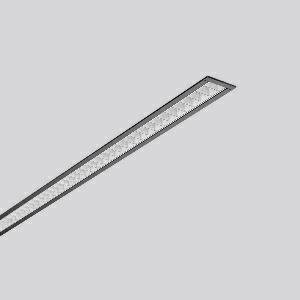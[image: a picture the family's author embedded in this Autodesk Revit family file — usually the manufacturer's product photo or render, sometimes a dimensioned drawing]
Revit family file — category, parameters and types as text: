
# Revit family: less_is_more_27_312177_003_1_6459
name_source: partatom
category: Lighting Fixtures
units: mm (PartAtom-declared; Revit-internal decimal feet)

## family parameters
Cut with Voids When Loaded = No
Host = Face
Light Source = No
Part Type = Normal
Room Calculation Point = No
Round Connector Dimension = Use Diameter
Shared = No

## types (1)
- LESS IS MORE 27 (1 x LED Modul 840, 2350 lm, 4000)
    Apparent Load = 25 VA
    CIE Flux Codes = 90 99 100 100 100
    Color Rendering = 80
    Color Temperature = 4000
    Default Elevation = 1800 mm
    Description = Series: LESS IS MORE 27
Recessed ceiling and wall luminaire with slim design. Housing: extruded aluminium profile, powder-coated. End cap aluminium powder-coated. High polish aluminium micro grid. Perfect for office areas (RUG < 19) and environments with computer screens in accordance with EN 12464-1. Suitable for Recessed ceiling mounting, wall (recessed). External driver with connecting cable. 
Colour: deep black, matt (RAL 9005)
Length: 1014 mm
Width: 38 mm
Height: 2 mm
Cut-out length: 1006 mm
Cut-out width: 30 mm
Recess height: 45-60 mm
Luminaire: recess height: 37 mm
Lamp: LED
Socket: without socket
Colour temperature: 4000K
Colour rendering index (CRI): 82
System power: 25 W
Rated luminous flux: 2350 lm
Luminous efficiency: 94 lm/W
Control gear: Regulated power supply
Protection class: II
Type of protection: IP 20
    Height = 0 mm  [stored 0 ft]
    Lamp = 1 x LED Modul 840
    Lamp Light Flux = 2350 lm
    Lamp count = 1
    Length = 1014 mm
    Lifetime = 50000 h
    Luminous efficacy = 94 lm/W
    Manufacturer = RZB
    ModVariant = No
    Model = 312177.003.1
    Mounting Place = Ceiling, Wall
    Mounting Type = Recessed
    Number of Poles = 1
    OnlyDefault = Yes
    Power Factor = 1
    Product Name = LESS IS MORE 27
    Product group = Recessed LED linear luminaires
    ProductGroupID = 407
    Protection Class = Protection class II
    Protection Degree = IP 20
    RLX_Detail_Level = 1
    RLX_Emergency_Light_Flux = 0 lm
    RLX_Emergency_Type = 0
    RLX_Emergency_Type_DB = No
    RlxData = <blob elided: 29905 chars, md5=71231851>
    Socket = socket
    Standby Power = 0 W
    System Light Flux = 2350 lm
    System Power = 25 W
    Type Comments = Product without accessories
    Type Image = 312177.003.jpg
    URL = http://relux.com
    VarID = ---
    Voltage = 230 V
    Voltage Range = 220-240 V
    Weight = 0.00 kg
    Width = 38 mm

note: [stored X ft] marks values corroborated as IEEE doubles in the binary element streams (Revit-internal decimal feet)

## geometry (parser evidence)
native form markers: Blend x4, Sweep x10
no freeform markers — native parametric forms only
